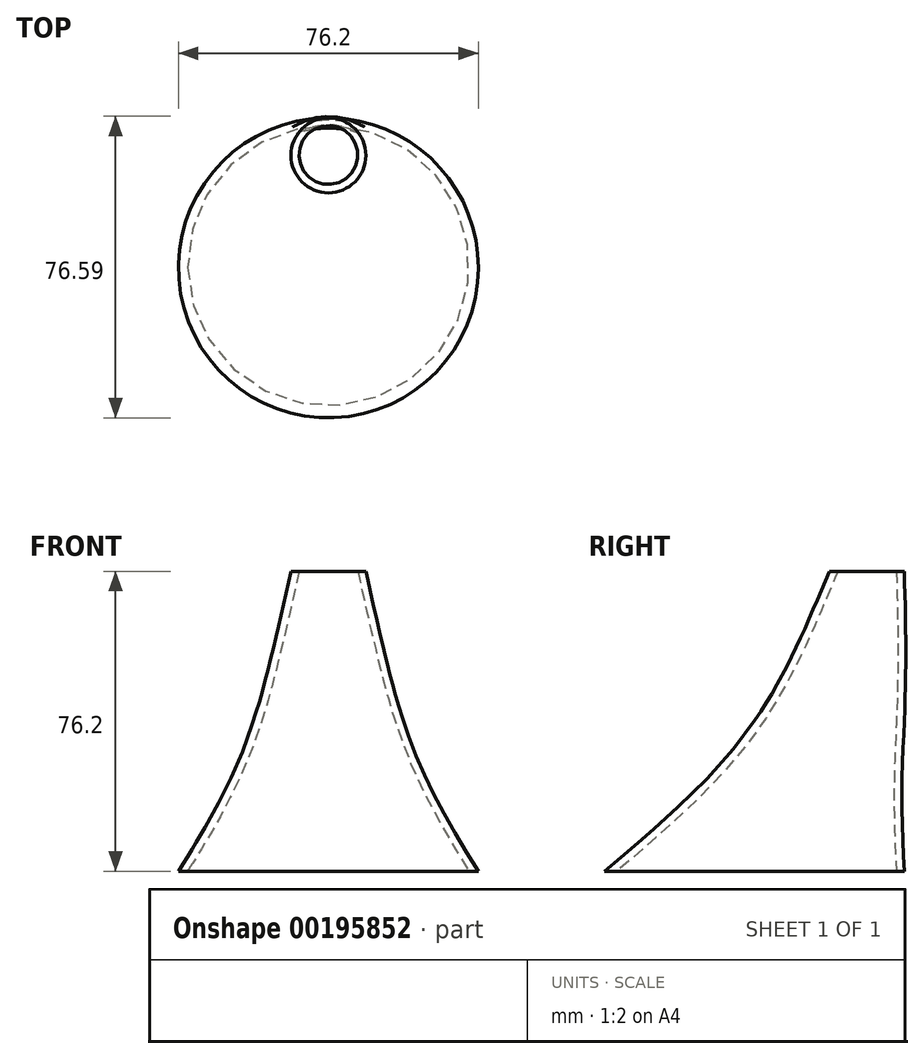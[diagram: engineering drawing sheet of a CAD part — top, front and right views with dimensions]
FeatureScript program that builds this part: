
annotation { "Feature Type Name" : "Feature", "Feature Type Description" : "" }
export const myFeature = defineFeature(function(context is Context, id is Id, definition is map)
    precondition{}
    {
        {
            var Q0;
            Q0=qCreatedBy(makeId("Top.planeOp"),FACE);
            var sketch = newSketch(context, id + "F0", { "sketchPlane" : qUnion([Q0])});
            skCircle(sketch, "E0", {"center": v(0, 0) * mm, "radius": 38.1 * mm});
            skSolve(sketch);
        }
        {
            var Q0;
            Q0=qCreatedBy(makeId("Top.planeOp"),FACE);
            cPlane(context, id + "F1", {"entities" : qUnion([Q0]), "cplaneType" : CPlaneType.OFFSET, "offset" : 38.1 * mm, "width" : 150 * mm, "height" : 150 * mm});
        }
        {
            var Q0;
            Q0=qCreatedBy(makeId("Top.planeOp"),FACE);
            cPlane(context, id + "F2", {"entities" : qUnion([Q0]), "cplaneType" : CPlaneType.OFFSET, "offset" : 76.2 * mm, "width" : 150 * mm, "height" : 150 * mm});
        }
        {
            var Q0;
            Q0=qCreatedBy(id+"F1.planeOp",FACE);
            var sketch = newSketch(context, id + "F3", { "sketchPlane" : qUnion([Q0])});
            skCircle(sketch, "E1", {"center": v(0, 19.05) * mm, "radius": 19.05 * mm});
            skSolve(sketch);
        }
        {
            var Q0;
            Q0=qCreatedBy(id+"F2.planeOp",FACE);
            var sketch = newSketch(context, id + "F4", { "sketchPlane" : qUnion([Q0])});
            skCircle(sketch, "E2", {"center": v(0, 28.58) * mm, "radius": 9.53 * mm});
            skSolve(sketch);
        }
        {
            var Q0;
            Q0=qCreatedBy(makeId("Right.planeOp"),FACE);
            var sketch = newSketch(context, id + "F5", { "sketchPlane" : qUnion([Q0])});
            skLineSegment(sketch, "E3", {"start": v(38.1, 0) * mm, "end": v(38.1, 76.2) * mm, "construction": true});
            skLineSegment(sketch, "E4", {"start": v(-38.1, 0) * mm, "end": v(0, 38.1) * mm, "construction": true});
            skLineSegment(sketch, "E5", {"start": v(0, 38.1) * mm, "end": v(19.05, 76.2) * mm, "construction": true});
            skSolve(sketch);
        }
        {
            var Q0;
            Q0=makeQuery(id+"F0.imprint","IMPRINT",FACE,{"disambiguationData":[TD([[makeQuery(id+"F0.imprint","IMPRINT",EDGE,{"derivedFrom":sQuery(id+"F0.wireOp",EDGE,"E0")}),1.0]])]});
            var Q1;
            Q1=makeQuery(id+"F3.imprint","IMPRINT",FACE,{"disambiguationData":[TD([[makeQuery(id+"F3.imprint","IMPRINT",EDGE,{"derivedFrom":sQuery(id+"F3.wireOp",EDGE,"E1")}),1.0]])]});
            var Q2;
            Q2=makeQuery(id+"F4.imprint","IMPRINT",FACE,{"disambiguationData":[TD([[makeQuery(id+"F4.imprint","IMPRINT",EDGE,{"derivedFrom":sQuery(id+"F4.wireOp",EDGE,"E2")}),1.0]])]});
            var Q3;
            Q3 = qConstructionFilter(qBodyType(qCreatedBy(id + "F5" ,EDGE), BodyType.WIRE), ConstructionObject.NO);
            loft(context, id + "F6", {"addGuides" : true, "sheetProfilesArray" : [{ "sheetProfileEntities" : qUnion([Q0]) }, { "sheetProfileEntities" : qUnion([Q1]) }, { "sheetProfileEntities" : qUnion([Q2]) }], "guidesArray" : [{ "guideEntities" : qUnion([Q3]), "guideDerivativeType" : LoftGuideDerivativeType.DEFAULT, "guideDerivativeMagnitude" : 1 }]});
        }
        {
            var Q0;
            Q0=makeQuery(id+"F6.opLoft","CAP_FACE",FACE,{"disambiguationData":[OSD([makeQuery(id+"F0.imprint","IMPRINT",FACE,{"disambiguationData":[TD([[makeQuery(id+"F0.imprint","IMPRINT",EDGE,{"derivedFrom":sQuery(id+"F0.wireOp",EDGE,"E0")}),1.0]])]})])],"isStart":true});
            var Q1;
            Q1=makeQuery(id+"F6.opLoft","CAP_FACE",FACE,{"disambiguationData":[OSD([makeQuery(id+"F4.imprint","IMPRINT",FACE,{"disambiguationData":[TD([[makeQuery(id+"F4.imprint","IMPRINT",EDGE,{"derivedFrom":sQuery(id+"F4.wireOp",EDGE,"E2")}),1.0]])]})])],"isStart":true});
            shell(context, id + "F7", {"entities" : qUnion([Q0, Q1]), "thickness" : 2 * mm});
        }
    });
